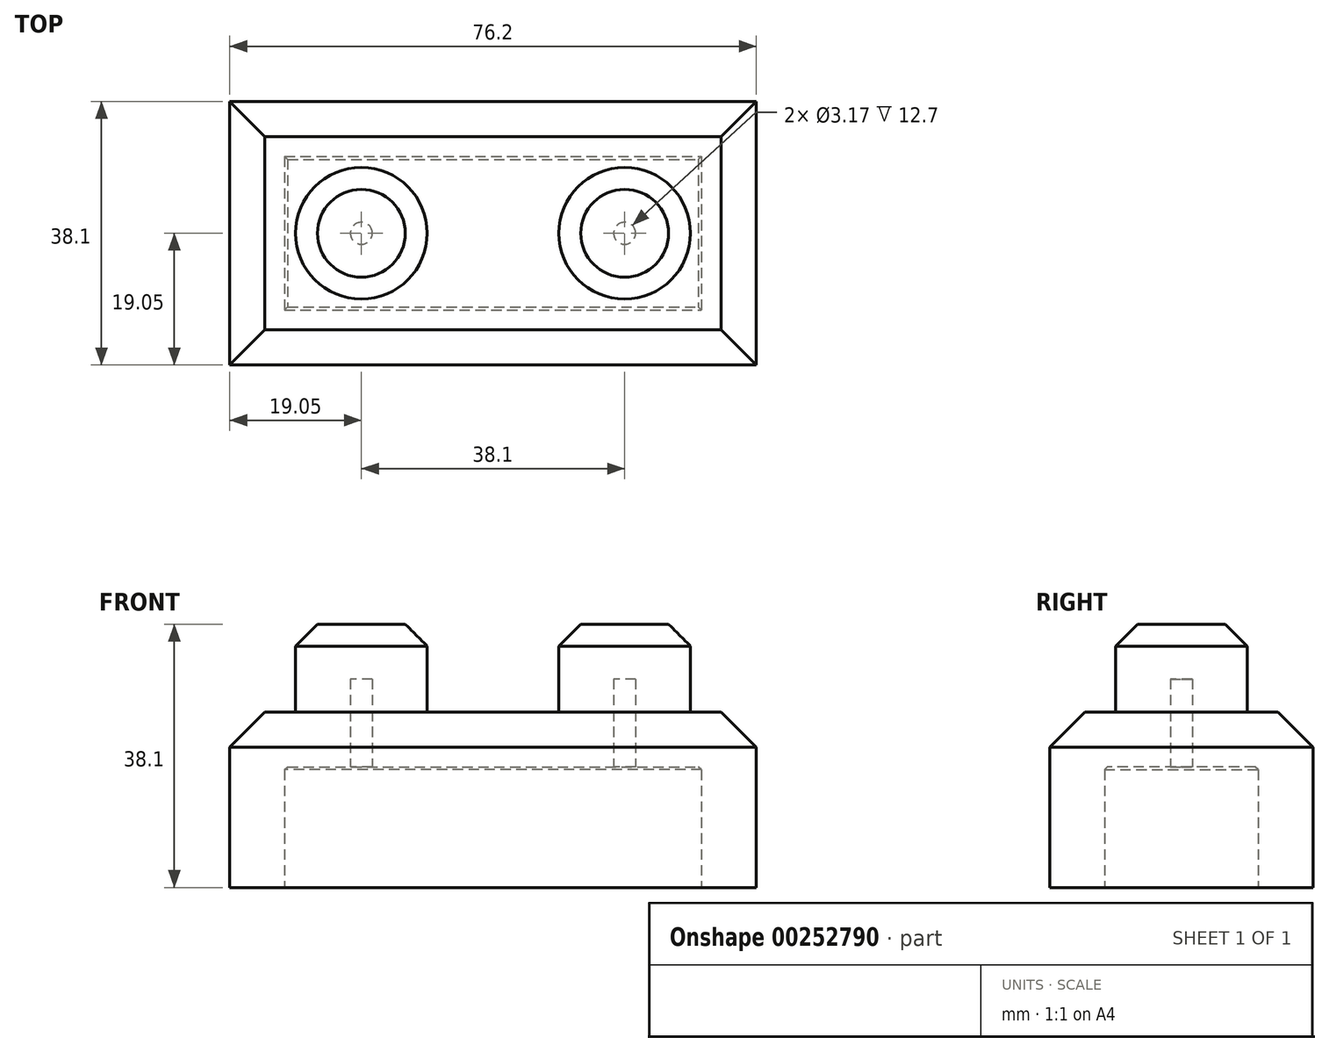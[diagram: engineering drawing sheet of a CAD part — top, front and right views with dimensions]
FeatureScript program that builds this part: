
annotation { "Feature Type Name" : "Feature", "Feature Type Description" : "" }
export const myFeature = defineFeature(function(context is Context, id is Id, definition is map)
    precondition{}
    {
        {
            var Q0;
            Q0=qCreatedBy(makeId("Top.planeOp"),FACE);
            var sketch = newSketch(context, id + "F0", { "sketchPlane" : qUnion([Q0])});
            skLineSegment(sketch, "E0.bottom", {"start": v(0, 0) * mm, "end": v(76.2, 0) * mm});
            skLineSegment(sketch, "E0.top", {"start": v(0, -38.1) * mm, "end": v(76.2, -38.1) * mm});
            skLineSegment(sketch, "E0.left", {"start": v(0, 0) * mm, "end": v(0, -38.1) * mm});
            skLineSegment(sketch, "E0.right", {"start": v(76.2, 0) * mm, "end": v(76.2, -38.1) * mm});
            skSolve(sketch);
        }
        {
            var Q0;
            Q0 = qSketchRegion(id + "F0", true);
            extrude(context, id + "F1", {"entities" : qUnion([Q0]), "depth" : 25.4 * mm});
        }
        {
            var Q0;
            Q0=makeQuery(id+"F1.opExtrude","CAP_EDGE",EDGE,{"disambiguationData":[OSD([sQuery(id+"F0.wireOp",EDGE,"E0.top")])],"isStart":false});
            var Q1;
            Q1=makeQuery(id+"F1.opExtrude","CAP_EDGE",EDGE,{"disambiguationData":[OSD([sQuery(id+"F0.wireOp",EDGE,"E0.right")])],"isStart":false});
            var Q2;
            Q2=makeQuery(id+"F1.opExtrude","CAP_EDGE",EDGE,{"disambiguationData":[OSD([sQuery(id+"F0.wireOp",EDGE,"E0.bottom")])],"isStart":false});
            var Q3;
            Q3=makeQuery(id+"F1.opExtrude","CAP_EDGE",EDGE,{"disambiguationData":[OSD([sQuery(id+"F0.wireOp",EDGE,"E0.left")])],"isStart":false});
            chamfer(context, id + "F2", {"entities" : qUnion([Q0, Q1, Q2, Q3]), "width" : 5.08 * mm, "tangentPropagation" : true});
        }
        {
            var Q0;
            Q0=makeQuery(id+"F1.opExtrude","CAP_FACE",FACE,{"disambiguationData":[OSD([sQuery(id+"F0.wireOp",EDGE,"E0.bottom"),sQuery(id+"F0.wireOp",EDGE,"E0.top"),sQuery(id+"F0.wireOp",EDGE,"E0.left"),sQuery(id+"F0.wireOp",EDGE,"E0.right")])],"isStart":false});
            var sketch = newSketch(context, id + "F3", { "sketchPlane" : qUnion([Q0])});
            skCircle(sketch, "E1", {"center": v(19.05, -19.05) * mm, "radius": 9.53 * mm});
            skCircle(sketch, "E2", {"center": v(57.15, -19.05) * mm, "radius": 9.53 * mm});
            skSolve(sketch);
        }
        {
            var Q0;
            Q0=makeQuery(id+"F3.imprint","IMPRINT",FACE,{"disambiguationData":[TD([[makeQuery(id+"F3.imprint","IMPRINT",EDGE,{"derivedFrom":sQuery(id+"F3.wireOp",EDGE,"E1")}),1.0]])]});
            var Q1;
            Q1=makeQuery(id+"F3.imprint","IMPRINT",FACE,{"disambiguationData":[TD([[makeQuery(id+"F3.imprint","IMPRINT",EDGE,{"derivedFrom":sQuery(id+"F3.wireOp",EDGE,"E2")}),1.0]])]});
            extrude(context, id + "F4", {"entities" : qUnion([Q0, Q1]), "operationType" : NewBodyOperationType.ADD, "depth" : 12.7 * mm});
        }
        {
            var Q0;
            Q0=makeQuery(id+"F4.opExtrude","CAP_EDGE",EDGE,{"disambiguationData":[OSD([sQuery(id+"F3.wireOp",EDGE,"E1")])],"isStart":false});
            var Q1;
            Q1=makeQuery(id+"F4.opExtrude","CAP_EDGE",EDGE,{"disambiguationData":[OSD([sQuery(id+"F3.wireOp",EDGE,"E2")])],"isStart":false});
            chamfer(context, id + "F5", {"entities" : qUnion([Q0, Q1]), "chamferType" : ChamferType.OFFSET_ANGLE, "width" : 3.17 * mm, "oppositeDirection" : false, "angle" : 45 * degree, "tangentPropagation" : true});
        }
        {
            var Q0;
            Q0=makeQuery(id+"F1.opExtrude","CAP_FACE",FACE,{"disambiguationData":[OSD([sQuery(id+"F0.wireOp",EDGE,"E0.bottom"),sQuery(id+"F0.wireOp",EDGE,"E0.top"),sQuery(id+"F0.wireOp",EDGE,"E0.left"),sQuery(id+"F0.wireOp",EDGE,"E0.right")])],"isStart":true});
            shell(context, id + "F6", {"entities" : qUnion([Q0]), "thickness" : 7.94 * mm});
        }
    });
